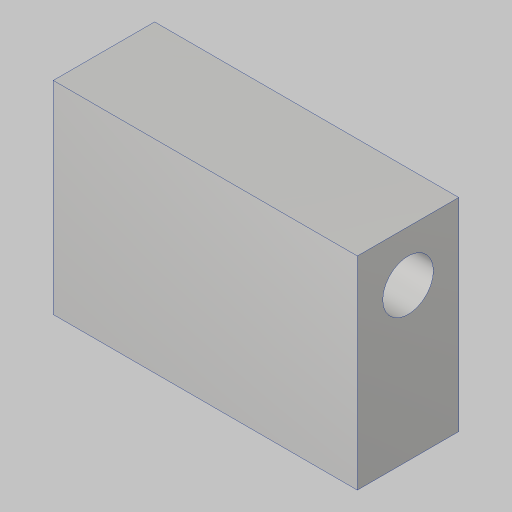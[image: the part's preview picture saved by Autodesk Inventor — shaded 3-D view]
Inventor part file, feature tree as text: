
AUTODESK INVENTOR PART (.ipt)
format: ipt  version: 2023.5 (Build 275446000, 446)  size: 119,808 bytes
history: native  units: in
note: dims shown in document units (in); Inventor stores cm internally (conversion verified against a paired STEP export)
features: sketch x3, hole x2, extrude x1
ambient origin geometry x8: Origin, YZ Plane, XZ Plane, XY Plane, X Axis, Y Axis, Z Axis, Center Point
bodies: Solid1 (feature_tree)
feature tree (6):
  extrude  "Extrusion1"  Depth=1.0in
  hole  "Hole1"  [1 undecoded]
  hole  "Hole2"  [1 undecoded]
  sketch  "Sketch1"  dims[d0=2.0in d1=1.0in]
  sketch  "Sketch2"  dims[d2=3.0in d3=0.0in d4=0.5in]
  sketch  "Sketch3"  dims[d5=0.5in d6=0.75in d7=0.385in d8=0.25in d9=0.5635in d10=1.0in d11=0.8108in d12=2.0in d13=0.156in d14=0.38in d15=0.375in d16=0.25in d17=0.5635in d18=1.0in d19=0.8108in]
note: 2 required parameter values undecoded (feature->parameter linkage not recoverable at this tier; creation-order binding heuristic only, values carry confidence <= 0.55)
